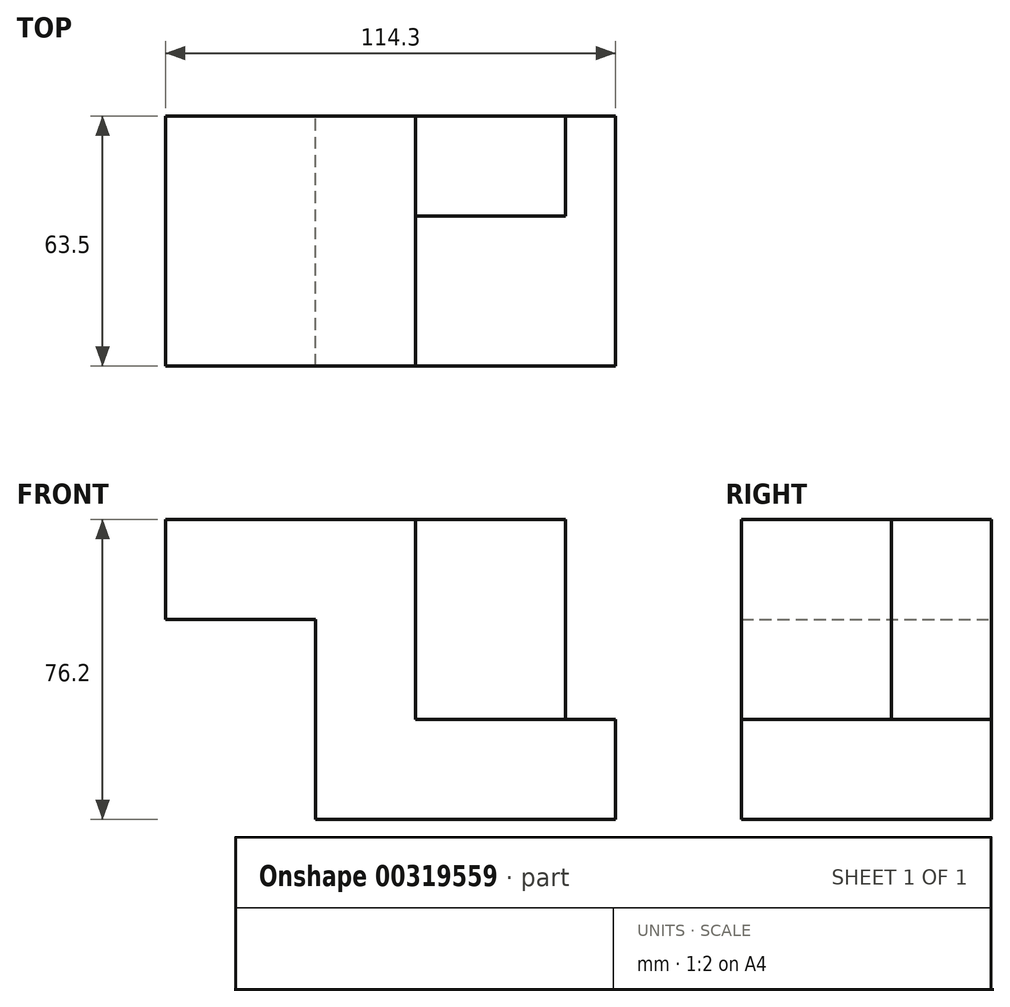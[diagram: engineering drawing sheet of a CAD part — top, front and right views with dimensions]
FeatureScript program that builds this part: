
annotation { "Feature Type Name" : "Feature", "Feature Type Description" : "" }
export const myFeature = defineFeature(function(context is Context, id is Id, definition is map)
    precondition{}
    {
        {
            var Q0;
            Q0=qCreatedBy(makeId("Front.planeOp"),FACE);
            var sketch = newSketch(context, id + "F0", { "sketchPlane" : qUnion([Q0])});
            skLineSegment(sketch, "E0", {"start": v(-57.01, 44.52) * mm, "end": v(6.49, 44.52) * mm});
            skLineSegment(sketch, "E1", {"start": v(6.49, 44.52) * mm, "end": v(6.49, -6.28) * mm});
            skLineSegment(sketch, "E2", {"start": v(6.49, -6.28) * mm, "end": v(57.29, -6.28) * mm});
            skLineSegment(sketch, "E3", {"start": v(57.29, -6.28) * mm, "end": v(57.29, -31.68) * mm});
            skLineSegment(sketch, "E4", {"start": v(57.29, -31.68) * mm, "end": v(-18.91, -31.68) * mm});
            skLineSegment(sketch, "E5", {"start": v(-18.91, -31.68) * mm, "end": v(-18.91, 19.12) * mm});
            skLineSegment(sketch, "E6", {"start": v(-18.91, 19.12) * mm, "end": v(-57.01, 19.12) * mm});
            skLineSegment(sketch, "E7", {"start": v(-57.01, 19.12) * mm, "end": v(-57.01, 44.52) * mm});
            skSolve(sketch);
        }
        {
            var Q0;
            Q0=makeQuery(id+"F0.imprint","IMPRINT",FACE,{"disambiguationData":[TD([[makeQuery(id+"F0.imprint","IMPRINT",EDGE,{"derivedFrom":sQuery(id+"F0.wireOp",EDGE,"E0")}),-1.0]])]});
            extrude(context, id + "F1", {"entities" : qUnion([Q0]), "depth" : 63.5 * mm});
        }
        {
            var Q0;
            Q0=makeQuery(id+"F1.opExtrude","CAP_FACE",FACE,{"disambiguationData":[OSD([sQuery(id+"F0.wireOp",EDGE,"E0"),sQuery(id+"F0.wireOp",EDGE,"E1"),sQuery(id+"F0.wireOp",EDGE,"E2"),sQuery(id+"F0.wireOp",EDGE,"E3"),sQuery(id+"F0.wireOp",EDGE,"E4"),sQuery(id+"F0.wireOp",EDGE,"E5"),sQuery(id+"F0.wireOp",EDGE,"E6"),sQuery(id+"F0.wireOp",EDGE,"E7")])],"isStart":true});
            var sketch = newSketch(context, id + "F2", { "sketchPlane" : qUnion([Q0])});
            skLineSegment(sketch, "E8", {"start": v(-6.49, 44.52) * mm, "end": v(-44.59, 44.52) * mm});
            skLineSegment(sketch, "E9", {"start": v(-44.59, 44.52) * mm, "end": v(-44.59, -6.28) * mm});
            skSolve(sketch);
        }
        {
            var Q0;
            Q0 = qSketchRegion(id + "F2", true);
            var Q1;
            Q1=makeQuery(id+"F2.imprint","IMPRINT",FACE,{"disambiguationData":[TD([[makeQuery(id+"F2.imprint","IMPRINT",EDGE,{"derivedFrom":sQuery(id+"F2.wireOp",EDGE,"E8")}),1.0]])]});
            extrude(context, id + "F3", {"entities" : qUnion([Q0, Q1]), "oppositeDirection" : true, "depth" : 25.4 * mm});
        }
    });
